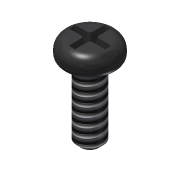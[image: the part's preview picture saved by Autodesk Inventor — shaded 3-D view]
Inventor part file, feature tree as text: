
AUTODESK INVENTOR PART (.ipt)
format: ipt  version: 2014 (Build 180170000, 170)  size: 161,792 bytes
history: native  units: in
note: dims shown in document units (in); Inventor stores cm internally (conversion verified against a paired STEP export)
features: extrude x3, fillet x3, sketch x3, thread x1, chamfer x1
ambient origin geometry x8: Origin, YZ Plane, XZ Plane, XY Plane, X Axis, Y Axis, Z Axis, Center Point
bodies: Solid1 (feature_tree)
feature tree (11):
  extrude  "Extrusion1"  Depth=0.315in TaperAngle=0.0deg
  extrude  "Extrusion2"  Depth=0.0866in TaperAngle=0.0deg
  fillet  "Fillet1"  Radius=0.0276in
  fillet  "Fillet2"  Radius=0.0472in
  extrude  "Extrusion3"  Depth=0.3937in
  fillet  "Fillet3"  Radius=0.1575in
  thread  "Thread1"  [1 undecoded]
  chamfer  "Chamfer1"  Distance=0.0787in
  sketch  "Sketch1"  dims[d0=0.1142in d1=0.315in d2=0.0in]
  sketch  "Sketch2"  dims[d3=0.2283in d4=0.0866in d5=0.0in d6=0.0276in d7=0.0472in]
  sketch  "Sketch3"  dims[d8=0.0276in d9=0.1575in d10=0.1575in d11=0.0276in d12=0.0787in d13=-0.0687in d14=0.0118in d15=0.3937in d16=0.0in d17=0.0197in d18=0.0787in d19=45.0deg]
note: 1 required parameter value undecoded (feature->parameter linkage not recoverable at this tier; creation-order binding heuristic only, values carry confidence <= 0.55)
